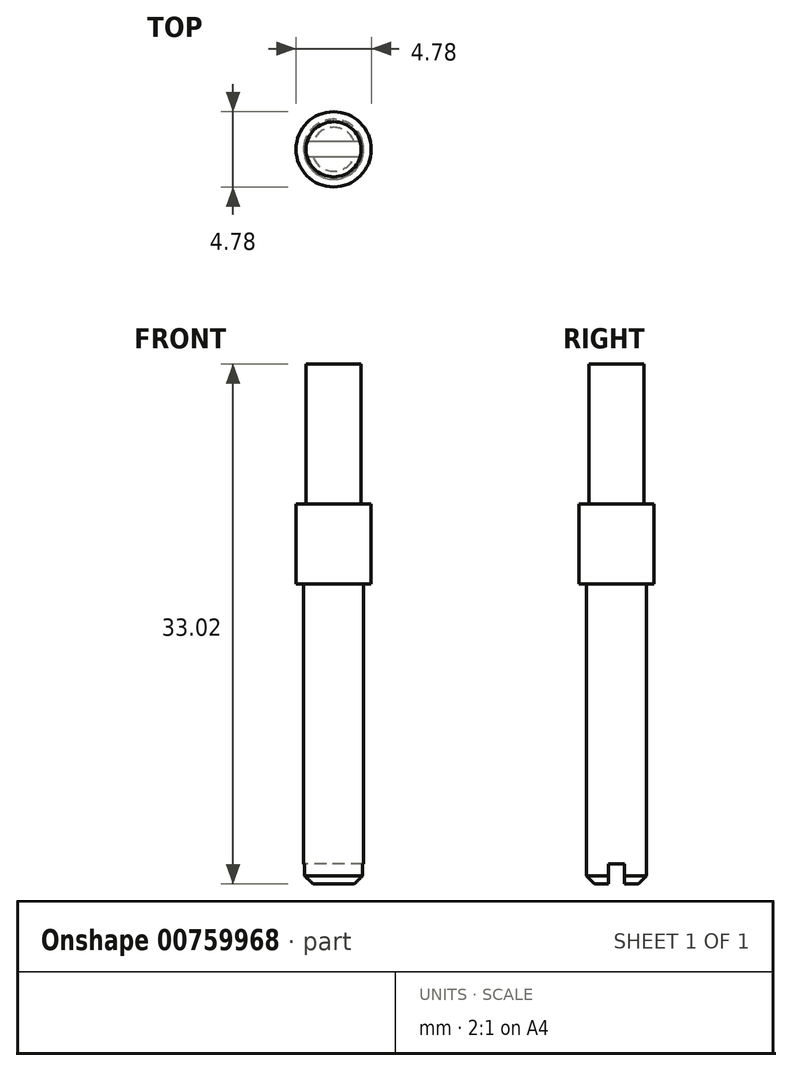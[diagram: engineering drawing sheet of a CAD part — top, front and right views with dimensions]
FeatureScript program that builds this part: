
annotation { "Feature Type Name" : "Feature", "Feature Type Description" : "" }
export const myFeature = defineFeature(function(context is Context, id is Id, definition is map)
    precondition{}
    {
        {
            var Q0;
            Q0=qCreatedBy(makeId("Top.planeOp"),FACE);
            var sketch = newSketch(context, id + "F0", { "sketchPlane" : qUnion([Q0])});
            skCircle(sketch, "E0", {"center": v(0, 0) * mm, "radius": 2.39 * mm});
            skSolve(sketch);
        }
        {
            var Q0;
            Q0=makeQuery(id+"F0.imprint","IMPRINT",FACE,{"disambiguationData":[TD([[makeQuery(id+"F0.imprint","IMPRINT",EDGE,{"derivedFrom":sQuery(id+"F0.wireOp",EDGE,"E0")}),1.0]])]});
            extrude(context, id + "F1", {"entities" : qUnion([Q0]), "depth" : 5.08 * mm, "offsetDistance" : 25.4 * mm});
        }
        {
            var Q0;
            Q0=makeQuery(id+"F1.opExtrude","CAP_FACE",FACE,{"disambiguationData":[OSD([sQuery(id+"F0.wireOp",EDGE,"E0")])],"isStart":false});
            var sketch = newSketch(context, id + "F2", { "sketchPlane" : qUnion([Q0])});
            skCircle(sketch, "E1", {"center": v(0, 0) * mm, "radius": 1.75 * mm});
            skSolve(sketch);
        }
        {
            var Q0;
            Q0=makeQuery(id+"F2.imprint","IMPRINT",FACE,{"disambiguationData":[TD([[makeQuery(id+"F2.imprint","IMPRINT",EDGE,{"derivedFrom":sQuery(id+"F2.wireOp",EDGE,"E1")}),1.0]])]});
            extrude(context, id + "F3", {"entities" : qUnion([Q0]), "operationType" : NewBodyOperationType.ADD, "depth" : 8.9 * mm, "offsetDistance" : 25.4 * mm});
        }
        {
            var Q0;
            Q0=makeQuery(id+"F1.opExtrude","CAP_FACE",FACE,{"disambiguationData":[OSD([sQuery(id+"F0.wireOp",EDGE,"E0")])],"isStart":true});
            var sketch = newSketch(context, id + "F4", { "sketchPlane" : qUnion([Q0])});
            skCircle(sketch, "E2", {"center": v(0, 0) * mm, "radius": 1.9 * mm});
            skSolve(sketch);
        }
        {
            var Q0;
            Q0=makeQuery(id+"F4.imprint","IMPRINT",FACE,{"disambiguationData":[TD([[makeQuery(id+"F4.imprint","IMPRINT",EDGE,{"derivedFrom":sQuery(id+"F4.wireOp",EDGE,"E2")}),1.0]])]});
            extrude(context, id + "F5", {"entities" : qUnion([Q0]), "operationType" : NewBodyOperationType.ADD, "depth" : 19.05 * mm, "offsetDistance" : 25.4 * mm});
        }
        {
            var Q0;
            Q0=makeQuery(id+"F5.opExtrude","CAP_EDGE",EDGE,{"disambiguationData":[OSD([sQuery(id+"F4.wireOp",EDGE,"E2")])],"isStart":false});
            chamfer(context, id + "F6", {"entities" : qUnion([Q0]), "width" : 0.5 * mm, "tangentPropagation" : true});
        }
        {
            var Q0;
            Q0=makeQuery(id+"F5.opExtrude","CAP_FACE",FACE,{"disambiguationData":[OSD([sQuery(id+"F4.wireOp",EDGE,"E2")])],"isStart":false});
            var sketch = newSketch(context, id + "F7", { "sketchPlane" : qUnion([Q0])});
            skLineSegment(sketch, "E3.bottom", {"start": v(4.36, -0.5) * mm, "end": v(-4.36, -0.5) * mm});
            skLineSegment(sketch, "E3.top", {"start": v(4.36, 0.5) * mm, "end": v(-4.36, 0.5) * mm});
            skLineSegment(sketch, "E3.left", {"start": v(4.36, -0.5) * mm, "end": v(4.36, 0.5) * mm});
            skLineSegment(sketch, "E3.right", {"start": v(-4.36, -0.5) * mm, "end": v(-4.36, 0.5) * mm});
            skPoint(sketch, "E3.middle", {"position": v(0, 0) * mm});
            skSolve(sketch);
        }
        {
            var Q0;
            Q0 = qSketchRegion(id + "F7", true);
            extrude(context, id + "F8", {"entities" : qUnion([Q0]), "operationType" : NewBodyOperationType.REMOVE, "oppositeDirection" : true, "depth" : 1.27 * mm, "offsetDistance" : 25.4 * mm});
        }
    });
